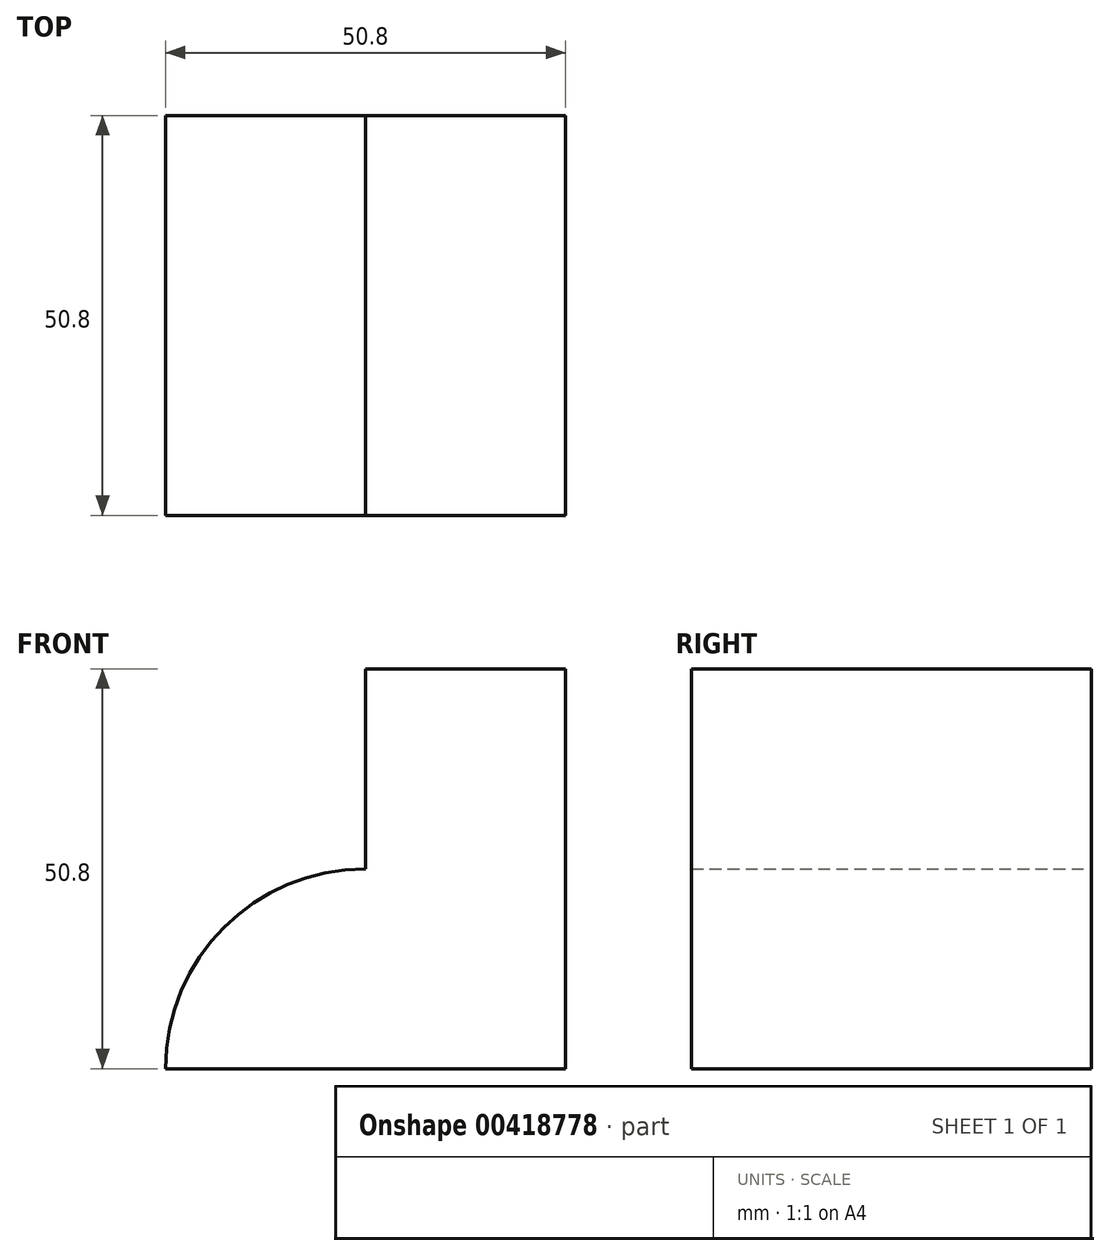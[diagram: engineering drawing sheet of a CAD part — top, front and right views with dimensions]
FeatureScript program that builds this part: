
annotation { "Feature Type Name" : "Feature", "Feature Type Description" : "" }
export const myFeature = defineFeature(function(context is Context, id is Id, definition is map)
    precondition{}
    {
        {
            var Q0;
            Q0=qCreatedBy(makeId("Front.planeOp"),FACE);
            var sketch = newSketch(context, id + "F0", { "sketchPlane" : qUnion([Q0])});
            skLineSegment(sketch, "E0", {"start": v(0, 0) * mm, "end": v(-50.8, 0) * mm});
            skArc(sketch, "E1", {"start": v(-25.4, 25.4) * mm, "mid": v(-43.36, 17.96) * mm, "end": v(-50.8, 0) * mm});
            skLineSegment(sketch, "E2", {"start": v(-25.4, 25.4) * mm, "end": v(-25.4, 50.8) * mm});
            skLineSegment(sketch, "E3", {"start": v(-25.4, 50.8) * mm, "end": v(0, 50.8) * mm});
            skLineSegment(sketch, "E4", {"start": v(0, 50.8) * mm, "end": v(0, 0) * mm});
            skSolve(sketch);
        }
        {
            var Q0;
            Q0 = qSketchRegion(id + "F0", true);
            extrude(context, id + "F1", {"entities" : qUnion([Q0]), "depth" : 50.8 * mm});
        }
    });
